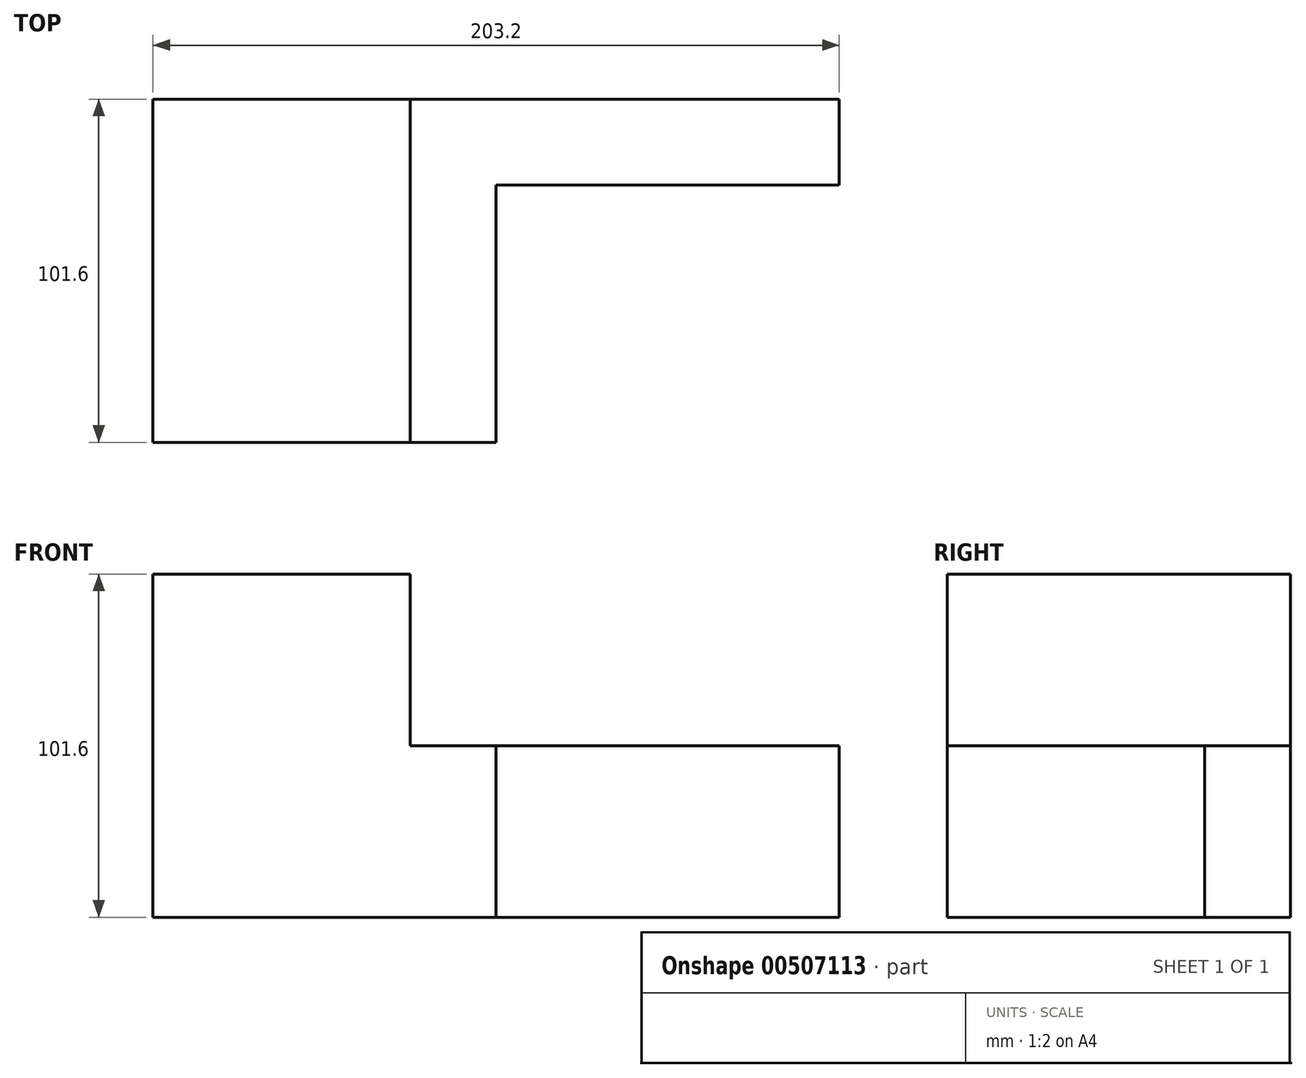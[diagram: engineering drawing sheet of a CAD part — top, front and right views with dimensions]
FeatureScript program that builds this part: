
annotation { "Feature Type Name" : "Feature", "Feature Type Description" : "" }
export const myFeature = defineFeature(function(context is Context, id is Id, definition is map)
    precondition{}
    {
        {
            var Q0;
            Q0=qCreatedBy(makeId("Top.planeOp"),FACE);
            var sketch = newSketch(context, id + "F0", { "sketchPlane" : qUnion([Q0])});
            skLineSegment(sketch, "E0.bottom", {"start": v(101.6, 50.8) * mm, "end": v(-101.6, 50.8) * mm});
            skLineSegment(sketch, "E0.top", {"start": v(101.6, -50.8) * mm, "end": v(-101.6, -50.8) * mm});
            skLineSegment(sketch, "E0.left", {"start": v(101.6, 50.8) * mm, "end": v(101.6, -50.8) * mm});
            skLineSegment(sketch, "E0.right", {"start": v(-101.6, 50.8) * mm, "end": v(-101.6, -50.8) * mm});
            skPoint(sketch, "E0.middle", {"position": v(0, 0) * mm});
            skSolve(sketch);
        }
        {
            var Q0;
            Q0 = qSketchRegion(id + "F0", true);
            extrude(context, id + "F1", {"entities" : qUnion([Q0]), "depth" : 101.6 * mm});
        }
        {
            var Q0;
            Q0=makeQuery(id+"F1.opExtrude","CAP_FACE",FACE,{"disambiguationData":[OSD([sQuery(id+"F0.wireOp",EDGE,"E0.bottom"),sQuery(id+"F0.wireOp",EDGE,"E0.top"),sQuery(id+"F0.wireOp",EDGE,"E0.left"),sQuery(id+"F0.wireOp",EDGE,"E0.right")])],"isStart":false});
            var sketch = newSketch(context, id + "F2", { "sketchPlane" : qUnion([Q0])});
            skLineSegment(sketch, "E1.bottom", {"start": v(101.6, 50.8) * mm, "end": v(-25.4, 50.8) * mm});
            skLineSegment(sketch, "E1.top", {"start": v(101.6, -50.8) * mm, "end": v(-25.4, -50.8) * mm});
            skLineSegment(sketch, "E1.left", {"start": v(101.6, 50.8) * mm, "end": v(101.6, -50.8) * mm});
            skLineSegment(sketch, "E1.right", {"start": v(-25.4, 50.8) * mm, "end": v(-25.4, -50.8) * mm});
            skSolve(sketch);
        }
        {
            var Q0;
            Q0 = qSketchRegion(id + "F2", true);
            extrude(context, id + "F3", {"entities" : qUnion([Q0]), "operationType" : NewBodyOperationType.REMOVE, "oppositeDirection" : true, "depth" : 50.8 * mm});
        }
        {
            var Q0;
            Q0=makeQuery(id+"F3.boolean.opBoolean","COPY",FACE,{"derivedFrom":makeQuery(id+"F3.opExtrude","CAP_FACE",FACE,{"disambiguationData":[OSD([sQuery(id+"F2.wireOp",EDGE,"E1.bottom"),sQuery(id+"F2.wireOp",EDGE,"E1.top"),sQuery(id+"F2.wireOp",EDGE,"E1.left"),sQuery(id+"F2.wireOp",EDGE,"E1.right")])],"isStart":false})});
            var sketch = newSketch(context, id + "F4", { "sketchPlane" : qUnion([Q0])});
            skLineSegment(sketch, "E2.bottom", {"start": v(101.6, -50.8) * mm, "end": v(0, -50.8) * mm});
            skLineSegment(sketch, "E2.top", {"start": v(101.6, 25.4) * mm, "end": v(0, 25.4) * mm});
            skLineSegment(sketch, "E2.left", {"start": v(101.6, -50.8) * mm, "end": v(101.6, 25.4) * mm});
            skLineSegment(sketch, "E2.right", {"start": v(0, -50.8) * mm, "end": v(0, 25.4) * mm});
            skSolve(sketch);
        }
        {
            var Q0;
            Q0=makeQuery(id+"F4.imprint","IMPRINT",FACE,{"disambiguationData":[TD([[makeQuery(id+"F4.imprint","IMPRINT",EDGE,{"derivedFrom":sQuery(id+"F4.wireOp",EDGE,"E2.bottom")}),-1.0]])]});
            extrude(context, id + "F5", {"entities" : qUnion([Q0]), "operationType" : NewBodyOperationType.REMOVE, "oppositeDirection" : true, "depth" : 50.8 * mm});
        }
    });
